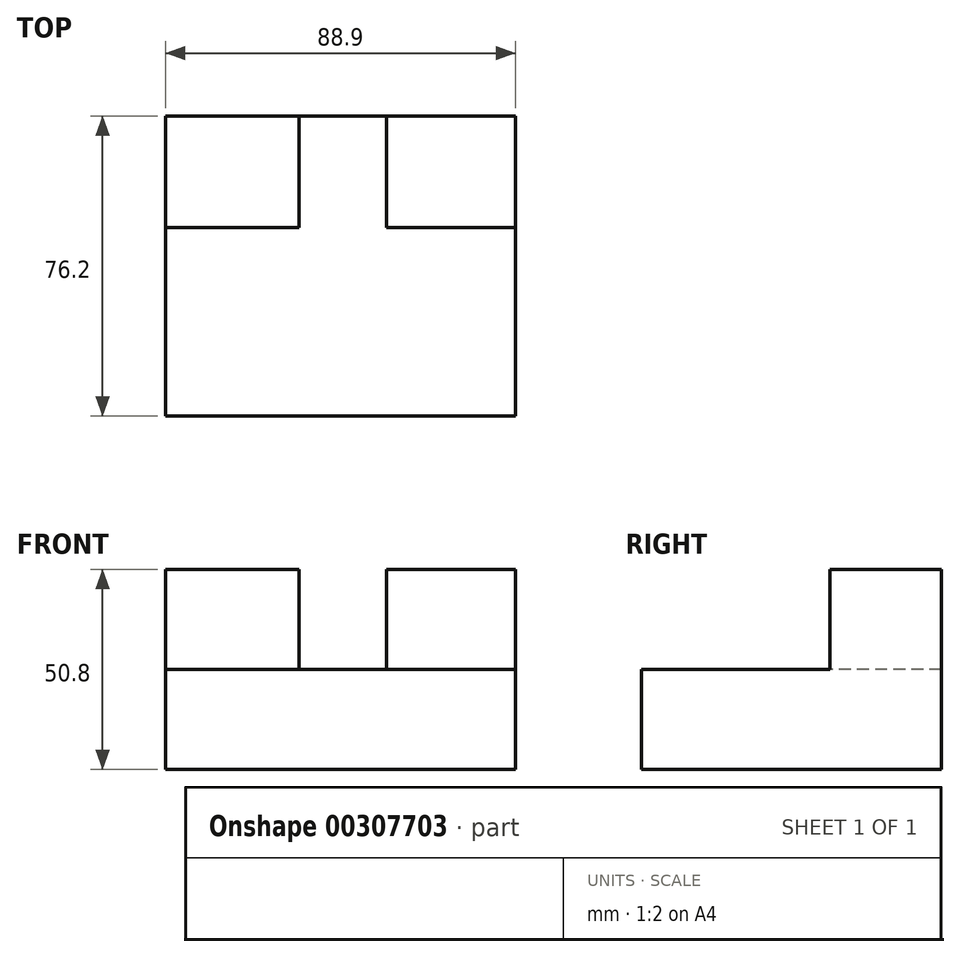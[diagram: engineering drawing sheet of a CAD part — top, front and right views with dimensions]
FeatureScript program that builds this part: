
annotation { "Feature Type Name" : "Feature", "Feature Type Description" : "" }
export const myFeature = defineFeature(function(context is Context, id is Id, definition is map)
    precondition{}
    {
        {
            var Q0;
            Q0=qCreatedBy(makeId("Top.planeOp"),FACE);
            var sketch = newSketch(context, id + "F0", { "sketchPlane" : qUnion([Q0])});
            skLineSegment(sketch, "E0", {"start": v(-42.71, -44.74) * mm, "end": v(46.19, -44.74) * mm});
            skLineSegment(sketch, "E1", {"start": v(46.19, -44.74) * mm, "end": v(46.19, 31.46) * mm});
            skLineSegment(sketch, "E2", {"start": v(46.19, 31.46) * mm, "end": v(-42.71, 31.46) * mm});
            skLineSegment(sketch, "E3", {"start": v(-42.71, 31.46) * mm, "end": v(-42.71, -44.74) * mm});
            skSolve(sketch);
        }
        {
            var Q0;
            Q0=makeQuery(id+"F0.imprint","IMPRINT",FACE,{"disambiguationData":[TD([[makeQuery(id+"F0.imprint","IMPRINT",EDGE,{"derivedFrom":sQuery(id+"F0.wireOp",EDGE,"E0")}),1.0]])]});
            extrude(context, id + "F1", {"entities" : qUnion([Q0]), "depth" : 25.4 * mm});
        }
        {
            var Q0;
            Q0=makeQuery(id+"F1.opExtrude","CAP_FACE",FACE,{"disambiguationData":[OSD([sQuery(id+"F0.wireOp",EDGE,"E0"),sQuery(id+"F0.wireOp",EDGE,"E1"),sQuery(id+"F0.wireOp",EDGE,"E2"),sQuery(id+"F0.wireOp",EDGE,"E3")])],"isStart":false});
            var sketch = newSketch(context, id + "F2", { "sketchPlane" : qUnion([Q0])});
            skLineSegment(sketch, "E4.bottom", {"start": v(-42.71, 31.46) * mm, "end": v(-8.82, 31.46) * mm});
            skLineSegment(sketch, "E4.top", {"start": v(-42.71, 3.16) * mm, "end": v(-8.82, 3.16) * mm});
            skLineSegment(sketch, "E4.left", {"start": v(-42.71, 31.46) * mm, "end": v(-42.71, 3.16) * mm});
            skLineSegment(sketch, "E4.right", {"start": v(-8.82, 31.46) * mm, "end": v(-8.82, 3.16) * mm});
            skLineSegment(sketch, "E5.bottom", {"start": v(46.19, 31.46) * mm, "end": v(13.42, 31.46) * mm});
            skLineSegment(sketch, "E5.top", {"start": v(46.19, 3.16) * mm, "end": v(13.42, 3.16) * mm});
            skLineSegment(sketch, "E5.left", {"start": v(46.19, 31.46) * mm, "end": v(46.19, 3.16) * mm});
            skLineSegment(sketch, "E5.right", {"start": v(13.42, 31.46) * mm, "end": v(13.42, 3.16) * mm});
            skSolve(sketch);
        }
        {
            var Q0;
            Q0=makeQuery(id+"F2.imprint","IMPRINT",FACE,{"disambiguationData":[TD([[makeQuery(id+"F2.imprint","IMPRINT",EDGE,{"derivedFrom":sQuery(id+"F2.wireOp",EDGE,"E4.bottom")}),1.0]])]});
            extrude(context, id + "F3", {"entities" : qUnion([Q0]), "operationType" : NewBodyOperationType.ADD, "depth" : 25.4 * mm});
        }
        {
            var Q0;
            Q0=makeQuery(id+"F2.imprint","IMPRINT",FACE,{"disambiguationData":[TD([[makeQuery(id+"F2.imprint","IMPRINT",EDGE,{"derivedFrom":sQuery(id+"F2.wireOp",EDGE,"E5.bottom")}),1.0]])]});
            extrude(context, id + "F4", {"entities" : qUnion([Q0]), "operationType" : NewBodyOperationType.ADD, "depth" : 25.4 * mm});
        }
    });
